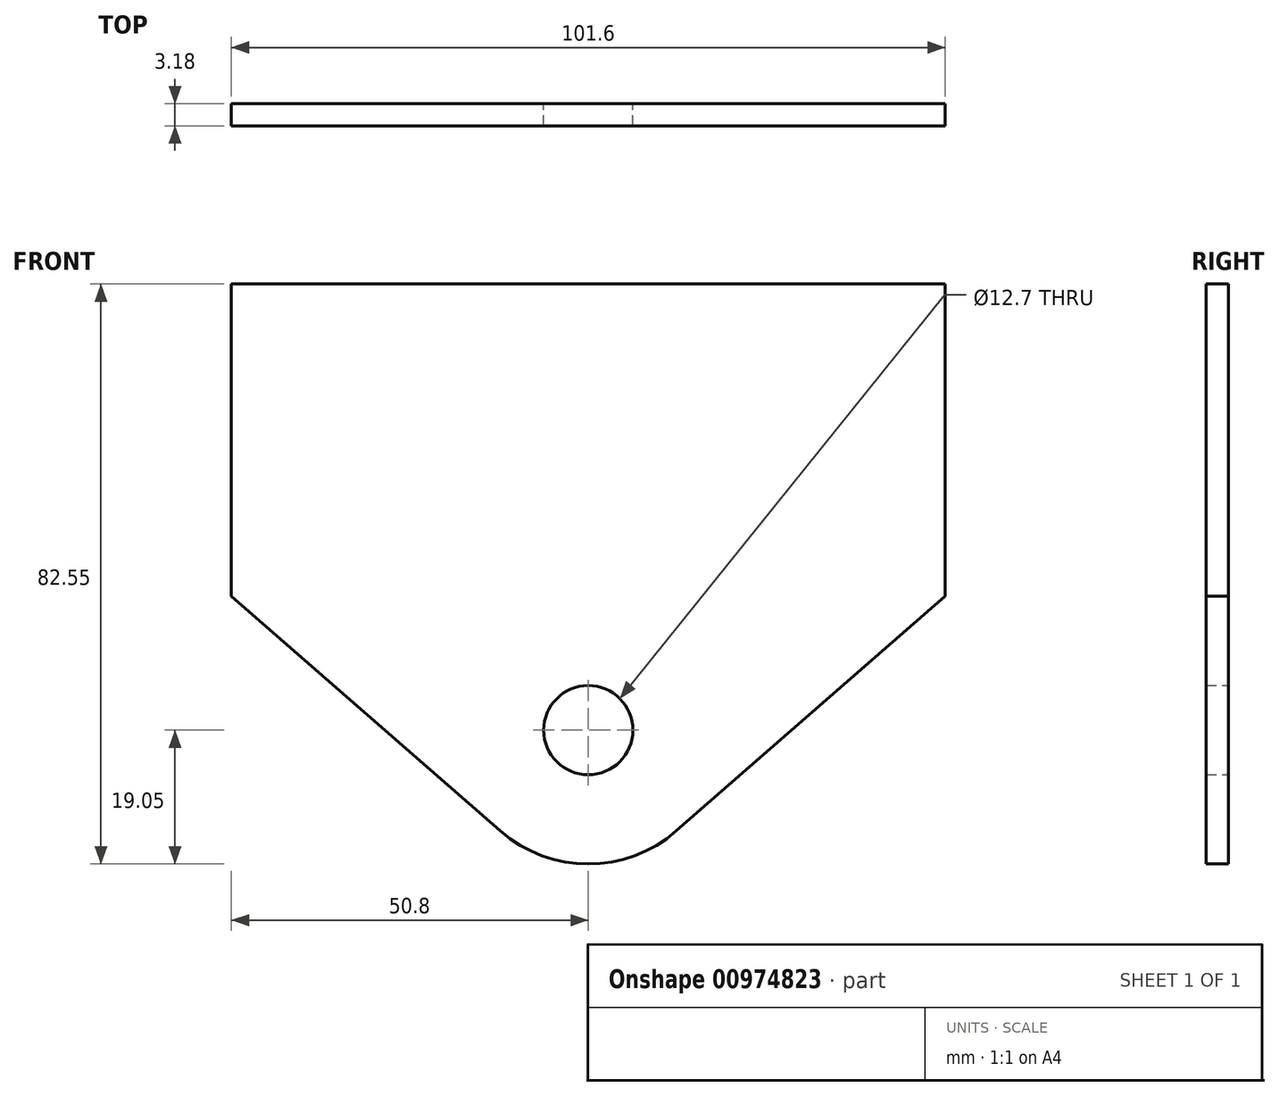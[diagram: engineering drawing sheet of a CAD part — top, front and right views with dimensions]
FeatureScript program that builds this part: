
annotation { "Feature Type Name" : "Feature", "Feature Type Description" : "" }
export const myFeature = defineFeature(function(context is Context, id is Id, definition is map)
    precondition{}
    {
        {
            var Q0;
            Q0=qCreatedBy(makeId("Front.planeOp"),FACE);
            var sketch = newSketch(context, id + "F0", { "sketchPlane" : qUnion([Q0])});
            skLineSegment(sketch, "E0.bottom", {"start": v(0, -25.4) * mm, "end": v(101.6, -25.4) * mm});
            skLineSegment(sketch, "E0.top", {"start": v(0, -69.85) * mm, "end": v(101.6, -69.85) * mm});
            skLineSegment(sketch, "E0.left", {"start": v(0, -25.4) * mm, "end": v(0, -69.85) * mm});
            skLineSegment(sketch, "E0.right", {"start": v(101.6, -25.4) * mm, "end": v(101.6, -69.85) * mm});
            skCircle(sketch, "E1", {"center": v(50.8, -88.9) * mm, "radius": 19.05 * mm});
            skLineSegment(sketch, "E2", {"start": v(0, -69.85) * mm, "end": v(38.27, -103.25) * mm});
            skLineSegment(sketch, "E3", {"start": v(101.6, -69.85) * mm, "end": v(63.33, -103.25) * mm});
            skCircle(sketch, "E4", {"center": v(50.8, -88.9) * mm, "radius": 6.35 * mm});
            skSolve(sketch);
        }
        {
            var Q0;
            Q0 = qSketchRegion(id + "F0", true);
            extrude(context, id + "F1", {"entities" : qUnion([Q0]), "depth" : 3.17 * mm, "offsetDistance" : 25.4 * mm});
        }
    });
